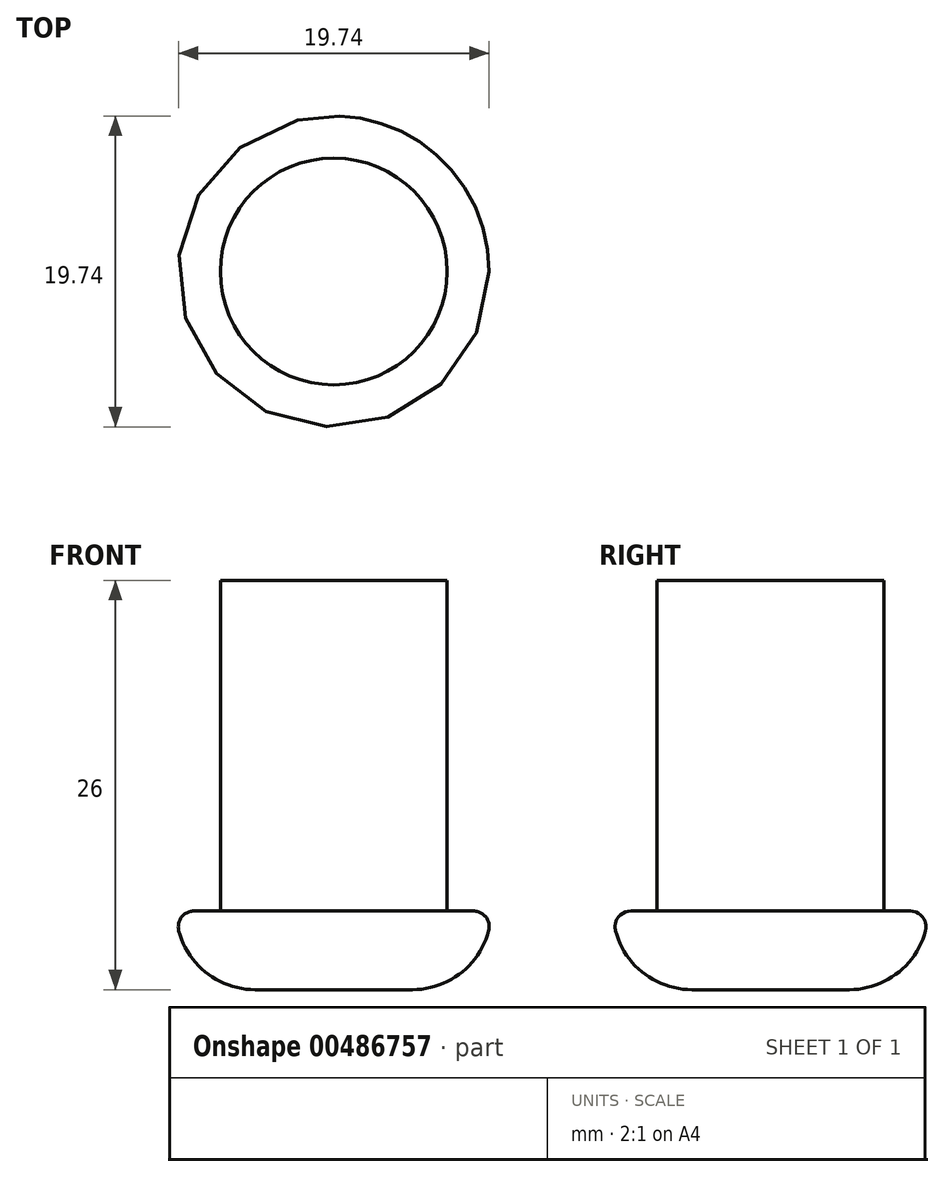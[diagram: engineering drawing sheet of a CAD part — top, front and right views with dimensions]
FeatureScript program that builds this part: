
annotation { "Feature Type Name" : "Feature", "Feature Type Description" : "" }
export const myFeature = defineFeature(function(context is Context, id is Id, definition is map)
    precondition{}
    {
        {
            var Q0;
            Q0=qCreatedBy(makeId("Top.planeOp"),FACE);
            var sketch = newSketch(context, id + "F0", { "sketchPlane" : qUnion([Q0])});
            skCircle(sketch, "E0", {"center": v(0, 0) * mm, "radius": 10 * mm});
            skSolve(sketch);
        }
        {
            var Q0;
            Q0 = qSketchRegion(id + "F0", true);
            extrude(context, id + "F1", {"entities" : qUnion([Q0]), "depth" : 5 * mm, "offsetDistance" : 25 * mm});
        }
        {
            var Q0;
            Q0=makeQuery(id+"F1.opExtrude","CAP_FACE",FACE,{"disambiguationData":[OSD([sQuery(id+"F0.wireOp",EDGE,"E0")])],"isStart":false});
            var sketch = newSketch(context, id + "F2", { "sketchPlane" : qUnion([Q0])});
            skCircle(sketch, "E1", {"center": v(0, 0) * mm, "radius": 7.2 * mm});
            skSolve(sketch);
        }
        {
            var Q0;
            Q0 = qSketchRegion(id + "F2", true);
            extrude(context, id + "F3", {"entities" : qUnion([Q0]), "operationType" : NewBodyOperationType.ADD, "depth" : 21 * mm, "offsetDistance" : 25 * mm});
        }
        {
            var Q0;
            Q0=makeQuery(id+"F1.opExtrude","CAP_EDGE",EDGE,{"disambiguationData":[OSD([sQuery(id+"F0.wireOp",EDGE,"E0")])],"isStart":true});
            fillet(context, id + "F4", {"entities" : qUnion([Q0]), "radius" : 5 * mm, "tangentPropagation" : true, "allowEdgeOverflow" : false});
        }
        {
            var Q0;
            {var subQ0=sQuery(id+"F0.wireOp",EDGE,"E0");Q0=makeQuery(id+"F4.opFillet","BLEND_EDGE",EDGE,{"blendedFrom":[makeQuery(id+"F1.opExtrude","CAP_EDGE",EDGE,{"disambiguationData":[OSD([subQ0])],"isStart":true}),makeQuery(id+"F1.opExtrude","CAP_FACE",FACE,{"disambiguationData":[OSD([subQ0])],"isStart":false})],"blendedInto":[makeQuery(id+"F1.opExtrude","CAP_FACE",FACE,{"disambiguationData":[OSD([subQ0])],"isStart":false})]});}
            fillet(context, id + "F5", {"entities" : qUnion([Q0]), "radius" : 1 * mm, "tangentPropagation" : true, "allowEdgeOverflow" : false});
        }
    });
